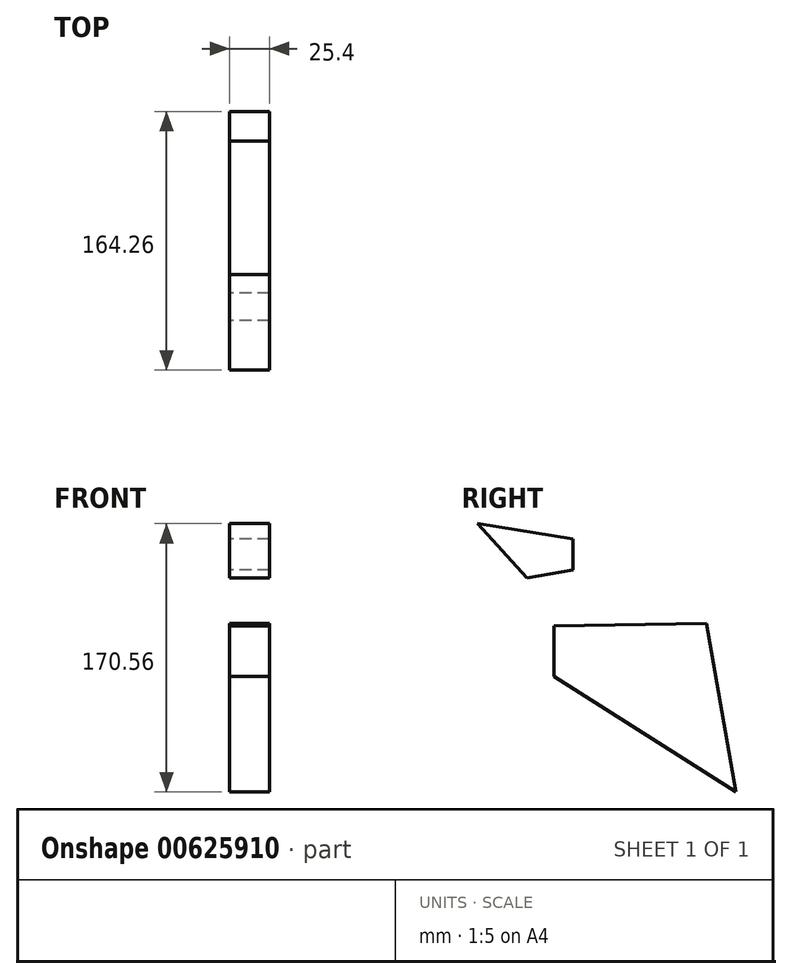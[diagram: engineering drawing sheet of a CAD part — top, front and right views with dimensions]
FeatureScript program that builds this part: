
annotation { "Feature Type Name" : "Feature", "Feature Type Description" : "" }
export const myFeature = defineFeature(function(context is Context, id is Id, definition is map)
    precondition{}
    {
        {
            var Q0;
            Q0=qCreatedBy(makeId("Right.planeOp"),FACE);
            var sketch = newSketch(context, id + "F0", { "sketchPlane" : qUnion([Q0])});
            skLineSegment(sketch, "E0", {"start": v(-96.75, 46.77) * mm, "end": v(-96.75, 14.73) * mm});
            skLineSegment(sketch, "E1", {"start": v(18.68, -58.8) * mm, "end": v(-96.75, 14.73) * mm});
            skLineSegment(sketch, "E2", {"start": v(18.68, -58.8) * mm, "end": v(0, 48.43) * mm});
            skLineSegment(sketch, "E3", {"start": v(0, 48.43) * mm, "end": v(-96.75, 46.77) * mm});
            skLineSegment(sketch, "E4", {"start": v(-69.37, 72.38) * mm, "end": v(-84.8, 82.21) * mm});
            skLineSegment(sketch, "E5", {"start": v(-84.8, 82.21) * mm, "end": v(-114.14, 77.1) * mm});
            skLineSegment(sketch, "E6", {"start": v(-114.14, 77.1) * mm, "end": v(-145.58, 111.77) * mm});
            skLineSegment(sketch, "E7", {"start": v(-145.58, 111.77) * mm, "end": v(-84.8, 102.14) * mm});
            skLineSegment(sketch, "E8", {"start": v(-84.8, 102.14) * mm, "end": v(-84.8, 82.21) * mm});
            skSolve(sketch);
        }
        {
            var Q0;
            Q0 = qSketchRegion(id + "F0", true);
            extrude(context, id + "F1", {"entities" : qUnion([Q0]), "depth" : 25.4 * mm, "offsetDistance" : 25.4 * mm});
        }
    });
